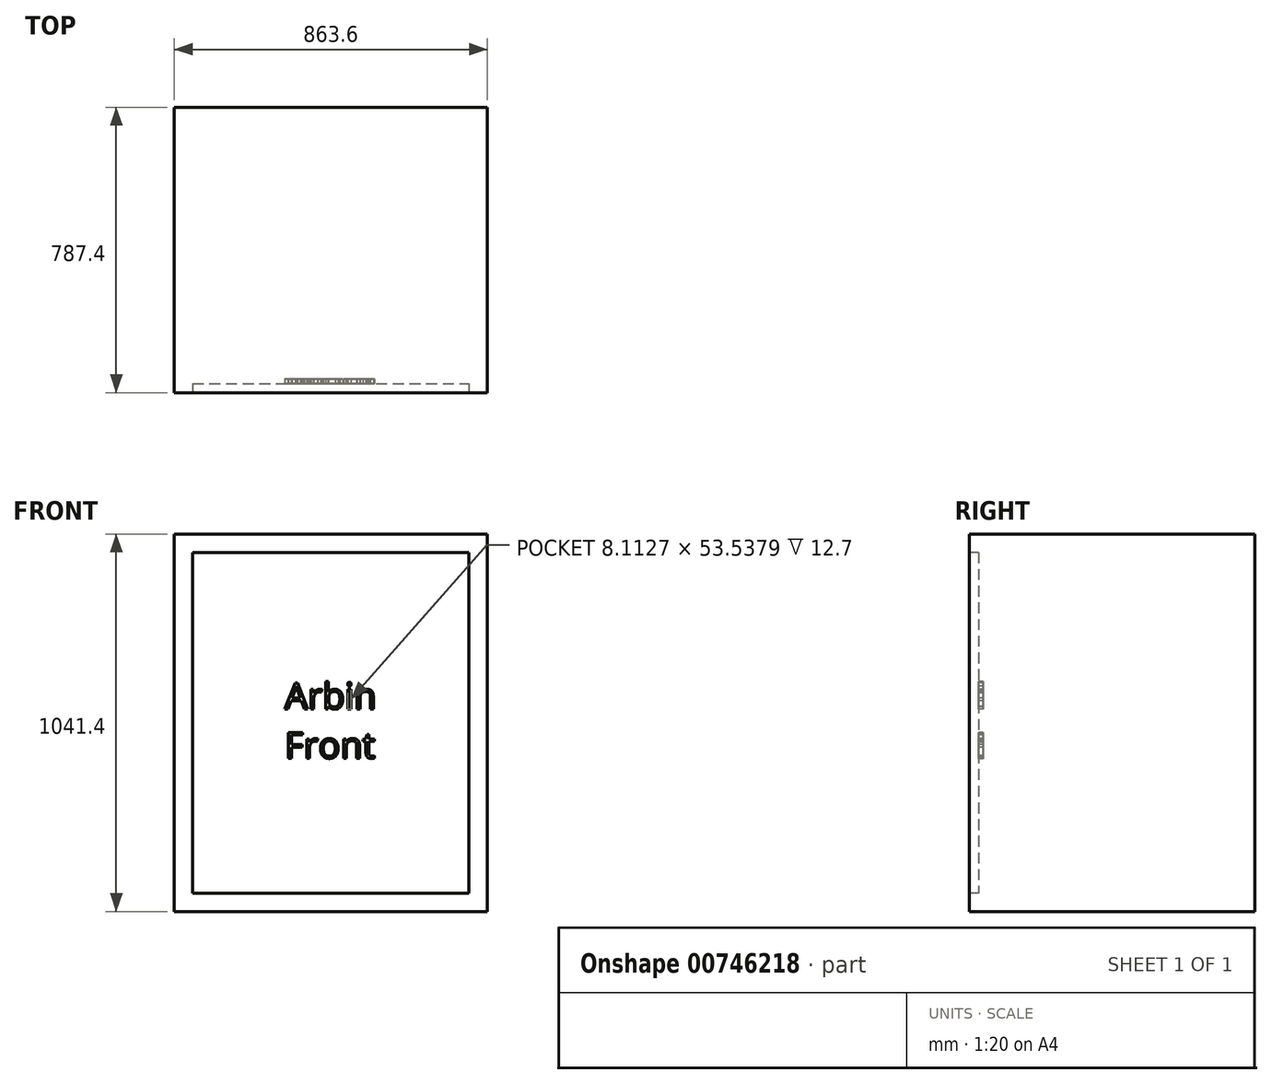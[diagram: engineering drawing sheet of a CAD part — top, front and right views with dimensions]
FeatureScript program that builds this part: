
annotation { "Feature Type Name" : "Feature", "Feature Type Description" : "" }
export const myFeature = defineFeature(function(context is Context, id is Id, definition is map)
    precondition{}
    {
        {
            var Q0;
            Q0=qCreatedBy(makeId("Top.planeOp"),FACE);
            var sketch = newSketch(context, id + "F0", { "sketchPlane" : qUnion([Q0])});
            skLineSegment(sketch, "E0.bottom", {"start": v(431.8, -393.7) * mm, "end": v(-431.8, -393.7) * mm});
            skLineSegment(sketch, "E0.top", {"start": v(431.8, 393.7) * mm, "end": v(-431.8, 393.7) * mm});
            skLineSegment(sketch, "E0.left", {"start": v(431.8, -393.7) * mm, "end": v(431.8, 393.7) * mm});
            skLineSegment(sketch, "E0.right", {"start": v(-431.8, -393.7) * mm, "end": v(-431.8, 393.7) * mm});
            skPoint(sketch, "E0.middle", {"position": v(0, 0) * mm});
            skSolve(sketch);
        }
        {
            var Q0;
            Q0=qSketchRegion(id+"F0",true);
            extrude(context, id + "F1", {"entities" : qUnion([Q0]), "depth" : 1041.4 * mm, "offsetDistance" : 25.4 * mm});
        }
        {
            var Q0;
            Q0=makeQuery(id+"F1.opExtrude","SWEPT_FACE",FACE,{"disambiguationData":[OSD([sQuery(id+"F0.wireOp",EDGE,"E0.bottom")])]});
            var sketch = newSketch(context, id + "F2", { "sketchPlane" : qUnion([Q0])});
            skLineSegment(sketch, "E1.bottom", {"start": v(-381, 990.6) * mm, "end": v(381, 990.6) * mm});
            skLineSegment(sketch, "E1.top", {"start": v(-381, 50.8) * mm, "end": v(381, 50.8) * mm});
            skLineSegment(sketch, "E1.left", {"start": v(-381, 990.6) * mm, "end": v(-381, 50.8) * mm});
            skLineSegment(sketch, "E1.right", {"start": v(381, 990.6) * mm, "end": v(381, 50.8) * mm});
            skSolve(sketch);
        }
        {
            var Q0;
            Q0=qSketchRegion(id+"F2",true);
            extrude(context, id + "F3", {"entities" : qUnion([Q0]), "operationType" : NewBodyOperationType.REMOVE, "oppositeDirection" : true, "depth" : 25.4 * mm, "offsetDistance" : 25.4 * mm});
        }
        {
            var Q0;
            Q0=makeQuery(id+"F3.boolean.opBoolean","COPY",FACE,{"derivedFrom":makeQuery(id+"F3.opExtrude","CAP_FACE",FACE,{"disambiguationData":[OSD([sQuery(id+"F2.wireOp",EDGE,"E1.bottom"),sQuery(id+"F2.wireOp",EDGE,"E1.top"),sQuery(id+"F2.wireOp",EDGE,"E1.left"),sQuery(id+"F2.wireOp",EDGE,"E1.right")])],"isStart":false})});
            var sketch = newSketch(context, id + "F4", { "sketchPlane" : qUnion([Q0])});
            skText(sketch, "E2", { "text": "Arbin \nFront\n", "fontName": "OpenSans-Regular.ttf"});
            const initialGuessF4  = {"E2": [-0.127, 0.5588, 1, 0, 0.07203]};
            skSetInitialGuess(sketch, initialGuessF4);
            skSolve(sketch);
        }
        {
            var Q0;
            Q0=qSketchRegion(id+"F4",true);
            extrude(context, id + "F5", {"entities" : qUnion([Q0]), "operationType" : NewBodyOperationType.REMOVE, "oppositeDirection" : true, "depth" : 12.7 * mm, "offsetDistance" : 25.4 * mm});
        }
    });
